# Revit family: LeL Tago 6.0
name_source: partatom
category: Lighting Fixtures
units: mm (PartAtom-declared; Revit-internal decimal feet)

## family parameters
Always vertical = No
Cut with Voids When Loaded = No
Light Source = No
OmniClass Number = 23.80.70.00
OmniClass Title = Lighting
Part Type = Normal
Room Calculation Point = No
Round Connector Dimension = Use Diameter
Shared = No
Work Plane-Based = Yes

## types (3) — shared parameters
Apparent Load = 14 VA
CCT = 4000 K
CRI = CRI80
Cable gland dimmable = Yes
Default Elevation = 1219 mm
Description = Outdoor/linear profiles
Finish = LeL Black
Hint = Switch on cable gland if dimmable
IK = IK09
IP = IP65 IP67 IP69
Lamp = LED
Manufacturer = L&L Luce&Light srl
Model = TG60
Rated Power supply = 48 V
URL = https://www.lucelight.it
Wattage = 14 W
Weight = 1.08 kg
zero-valued in all types: Clips offset

## per-type parameters (varying)
| type | Lumen Output | Optic |
| 6.0 S 24° 14W | 1374 lm | TAGO Light source : 6.0 S 24° 14W |
| 6.0 M 30° 14W | 1290 lm | TAGO Light source : 6.0 M 30° 14W |
| 6.0 L 52° 14W | 1206 lm | TAGO Light source : 6.0 L 52° 14W |

## geometry (parser evidence)
native form markers: Sweep x4
no freeform markers — native parametric forms only
